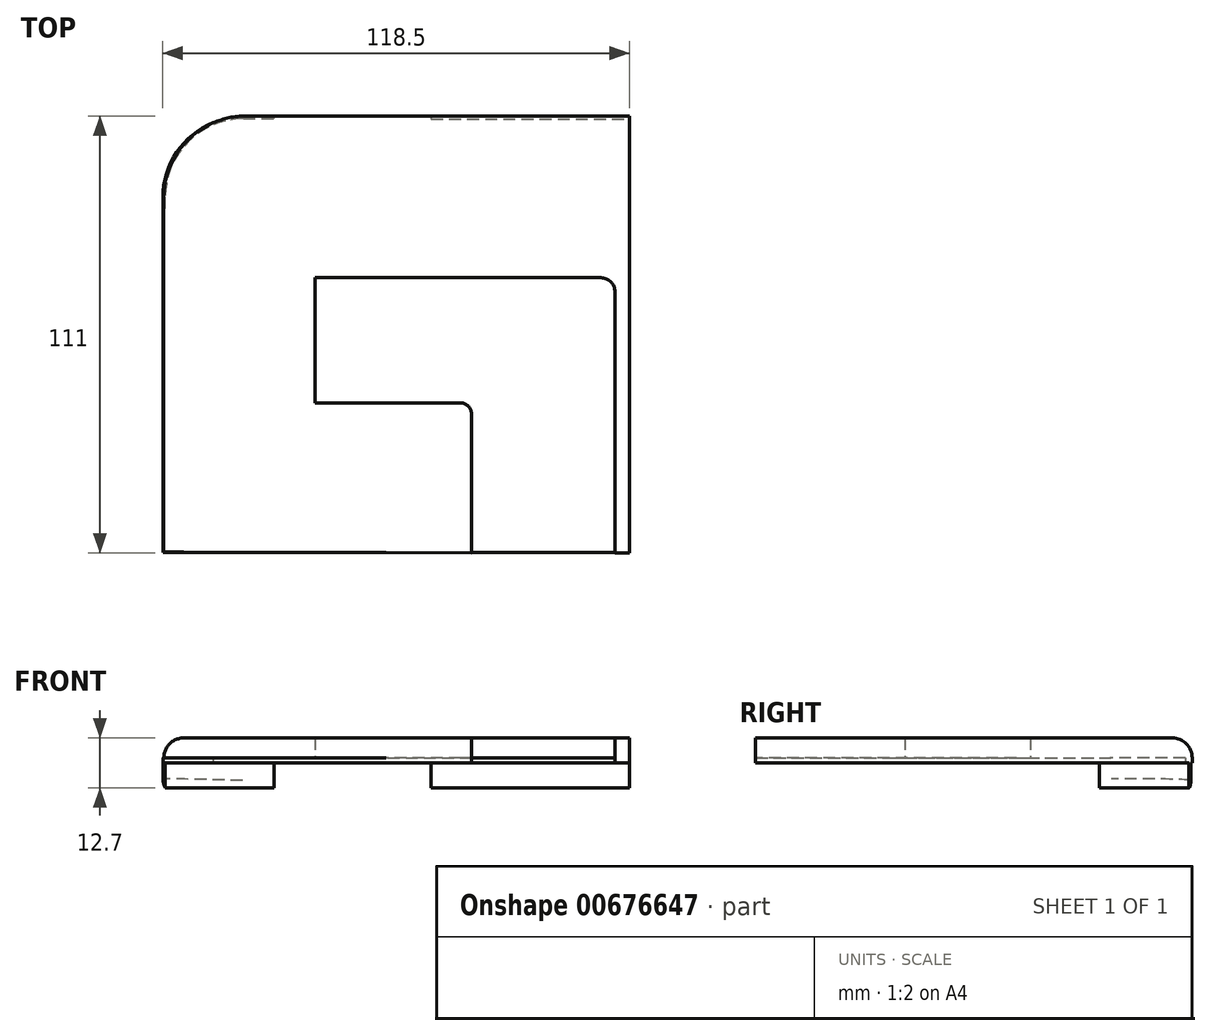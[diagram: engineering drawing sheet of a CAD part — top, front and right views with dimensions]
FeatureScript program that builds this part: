
annotation { "Feature Type Name" : "Feature", "Feature Type Description" : "" }
export const myFeature = defineFeature(function(context is Context, id is Id, definition is map)
    precondition{}
    {
        {
            var Q0;
            Q0=qCreatedBy(makeId("Top.planeOp"),FACE);
            var sketch = newSketch(context, id + "F0", { "sketchPlane" : qUnion([Q0])});
            skLineSegment(sketch, "E0", {"start": v(-57, -48.12) * mm, "end": v(-57, 42.23) * mm});
            skLineSegment(sketch, "E1", {"start": v(-57, -48.12) * mm, "end": v(61.23, -48.12) * mm});
            skLineSegment(sketch, "E2", {"start": v(61.23, -48.12) * mm, "end": v(61.23, 62.53) * mm});
            skLineSegment(sketch, "E3", {"start": v(61.23, 62.53) * mm, "end": v(-36.68, 62.55) * mm});
            skPoint(sketch, "E4.visualSharp", {"position": v(-57, 62.56) * mm});
            skArc(sketch, "E4.filletArc", {"start": v(-36.68, 62.55) * mm, "mid": v(-51.05, 56.6) * mm, "end": v(-57, 42.23) * mm});
            skSolve(sketch);
        }
        {
            var Q0;
            Q0 = qSketchRegion(id + "F0", true);
            extrude(context, id + "F1", {"entities" : qUnion([Q0]), "depth" : 1.27 * mm, "offsetDistance" : 25.4 * mm});
        }
        {
            var Q0;
            Q0=qCreatedBy(makeId("Top.planeOp"),FACE);
            var sketch = newSketch(context, id + "F2", { "sketchPlane" : qUnion([Q0])});
            skLineSegment(sketch, "E5", {"start": v(-28.79, 62.5) * mm, "end": v(-36.74, 62.5) * mm});
            skLineSegment(sketch, "E6", {"start": v(-56.99, 42.26) * mm, "end": v(-56.99, 39.26) * mm});
            skPoint(sketch, "E7.visualSharp", {"position": v(-56.99, 62.5) * mm});
            skArc(sketch, "E7.filletArc", {"start": v(-36.74, 62.5) * mm, "mid": v(-51.06, 56.57) * mm, "end": v(-56.99, 42.26) * mm});
            skLineSegment(sketch, "E8", {"start": v(-56.99, 39.26) * mm, "end": v(-56.99, 42.26) * mm});
            skLineSegment(sketch, "E9", {"start": v(-56.99, 39.26) * mm, "end": v(-56.41, 39.26) * mm});
            skLineSegment(sketch, "E10", {"start": v(-56.41, 39.26) * mm, "end": v(-56.41, 42.26) * mm});
            skLineSegment(sketch, "E11", {"start": v(-36.53, 62.14) * mm, "end": v(-28.8, 62.14) * mm});
            skLineSegment(sketch, "E12", {"start": v(-28.8, 62.14) * mm, "end": v(-28.79, 62.5) * mm});
            skPoint(sketch, "E13.visualSharp", {"position": v(-56.41, 62.14) * mm});
            skArc(sketch, "E13.filletArc", {"start": v(-36.53, 62.14) * mm, "mid": v(-50.59, 56.32) * mm, "end": v(-56.41, 42.26) * mm});
            skLineSegment(sketch, "E14", {"start": v(11.9, 62.48) * mm, "end": v(11.9, 61.96) * mm});
            skSolve(sketch);
        }
        {
            var Q0;
            Q0 = qSketchRegion(id + "F2", true);
            extrude(context, id + "F3", {"entities" : qUnion([Q0]), "operationType" : NewBodyOperationType.ADD, "depth" : -6.35 * mm, "offsetDistance" : 25.4 * mm});
        }
        {
            var Q0;
            Q0=makeQuery(id+"F3.opExtrude","CAP_EDGE",EDGE,{"disambiguationData":[OSD([sQuery(id+"F2.wireOp",EDGE,"E5")])],"isStart":false});
            fillet(context, id + "F4", {"entities" : qUnion([Q0]), "radius" : 5.08 * mm, "tangentPropagation" : true, "allowEdgeOverflow" : false});
        }
        {
            var Q0;
            Q0=qCreatedBy(makeId("Top.planeOp"),FACE);
            var sketch = newSketch(context, id + "F5", { "sketchPlane" : qUnion([Q0])});
            skLineSegment(sketch, "E15", {"start": v(61.5, 62.5) * mm, "end": v(11.12, 62.5) * mm});
            skLineSegment(sketch, "E16", {"start": v(11.12, 62.5) * mm, "end": v(11.12, 61.99) * mm});
            skLineSegment(sketch, "E17", {"start": v(11.12, 61.99) * mm, "end": v(61.5, 61.99) * mm});
            skLineSegment(sketch, "E18", {"start": v(61.5, 61.99) * mm, "end": v(61.5, 62.5) * mm});
            skSolve(sketch);
        }
        {
            var Q0;
            Q0 = qSketchRegion(id + "F5", true);
            extrude(context, id + "F6", {"entities" : qUnion([Q0]), "operationType" : NewBodyOperationType.ADD, "depth" : -6.35 * mm, "offsetDistance" : 25.4 * mm});
        }
        {
            var Q0;
            Q0=makeQuery(id+"F6.opExtrude","CAP_EDGE",EDGE,{"disambiguationData":[OSD([sQuery(id+"F5.wireOp",EDGE,"E15")])],"isStart":false});
            fillet(context, id + "F7", {"entities" : qUnion([Q0]), "radius" : 3.07 * mm, "tangentPropagation" : true, "allowEdgeOverflow" : false});
        }
        {
            var Q0;
            Q0=qCreatedBy(makeId("Top.planeOp"),FACE);
            var sketch = newSketch(context, id + "F8", { "sketchPlane" : qUnion([Q0])});
            skLineSegment(sketch, "E19", {"start": v(61.5, -48.17) * mm, "end": v(61.5, 62.83) * mm});
            skLineSegment(sketch, "E20", {"start": v(61.5, 62.83) * mm, "end": v(-35.91, 62.83) * mm});
            skLineSegment(sketch, "E21", {"start": v(-56.76, 41.98) * mm, "end": v(-56.76, -47.97) * mm});
            skLineSegment(sketch, "E22", {"start": v(61.5, -48.17) * mm, "end": v(57.87, -48.17) * mm});
            skLineSegment(sketch, "E23", {"start": v(57.87, -48.17) * mm, "end": v(57.87, 18.12) * mm});
            skLineSegment(sketch, "E24", {"start": v(54.26, 21.73) * mm, "end": v(-18.28, 21.73) * mm});
            skLineSegment(sketch, "E25", {"start": v(-18.28, 21.73) * mm, "end": v(-18.28, -10.1) * mm});
            skLineSegment(sketch, "E26", {"start": v(-18.28, -10.1) * mm, "end": v(18.69, -10.1) * mm});
            skLineSegment(sketch, "E27", {"start": v(21.4, -12.81) * mm, "end": v(21.4, -48.17) * mm});
            skLineSegment(sketch, "E28", {"start": v(21.4, -48.17) * mm, "end": v(-56.76, -47.97) * mm});
            skPoint(sketch, "E29.visualSharp", {"position": v(57.87, 21.73) * mm});
            skArc(sketch, "E29.filletArc", {"start": v(57.87, 18.12) * mm, "mid": v(56.81, 20.68) * mm, "end": v(54.26, 21.73) * mm});
            skPoint(sketch, "E30.visualSharp", {"position": v(-56.76, 62.83) * mm});
            skArc(sketch, "E30.filletArc", {"start": v(-35.91, 62.83) * mm, "mid": v(-50.66, 56.73) * mm, "end": v(-56.76, 41.98) * mm});
            skPoint(sketch, "E31.visualSharp", {"position": v(21.4, -10.1) * mm});
            skArc(sketch, "E31.filletArc", {"start": v(21.4, -12.81) * mm, "mid": v(20.6, -10.9) * mm, "end": v(18.69, -10.1) * mm});
            skSolve(sketch);
        }
        {
            var Q0;
            Q0 = qSketchRegion(id + "F8", true);
            extrude(context, id + "F9", {"entities" : qUnion([Q0]), "operationType" : NewBodyOperationType.ADD, "depth" : 6.35 * mm, "offsetDistance" : 25.4 * mm});
        }
        {
            var Q0;
            Q0=makeQuery(id+"F9.opExtrude","CAP_EDGE",EDGE,{"disambiguationData":[OSD([sQuery(id+"F8.wireOp",EDGE,"E20")])],"isStart":false});
            fillet(context, id + "F10", {"entities" : qUnion([Q0]), "radius" : 5.08 * mm, "tangentPropagation" : true, "allowEdgeOverflow" : false});
        }
    });
